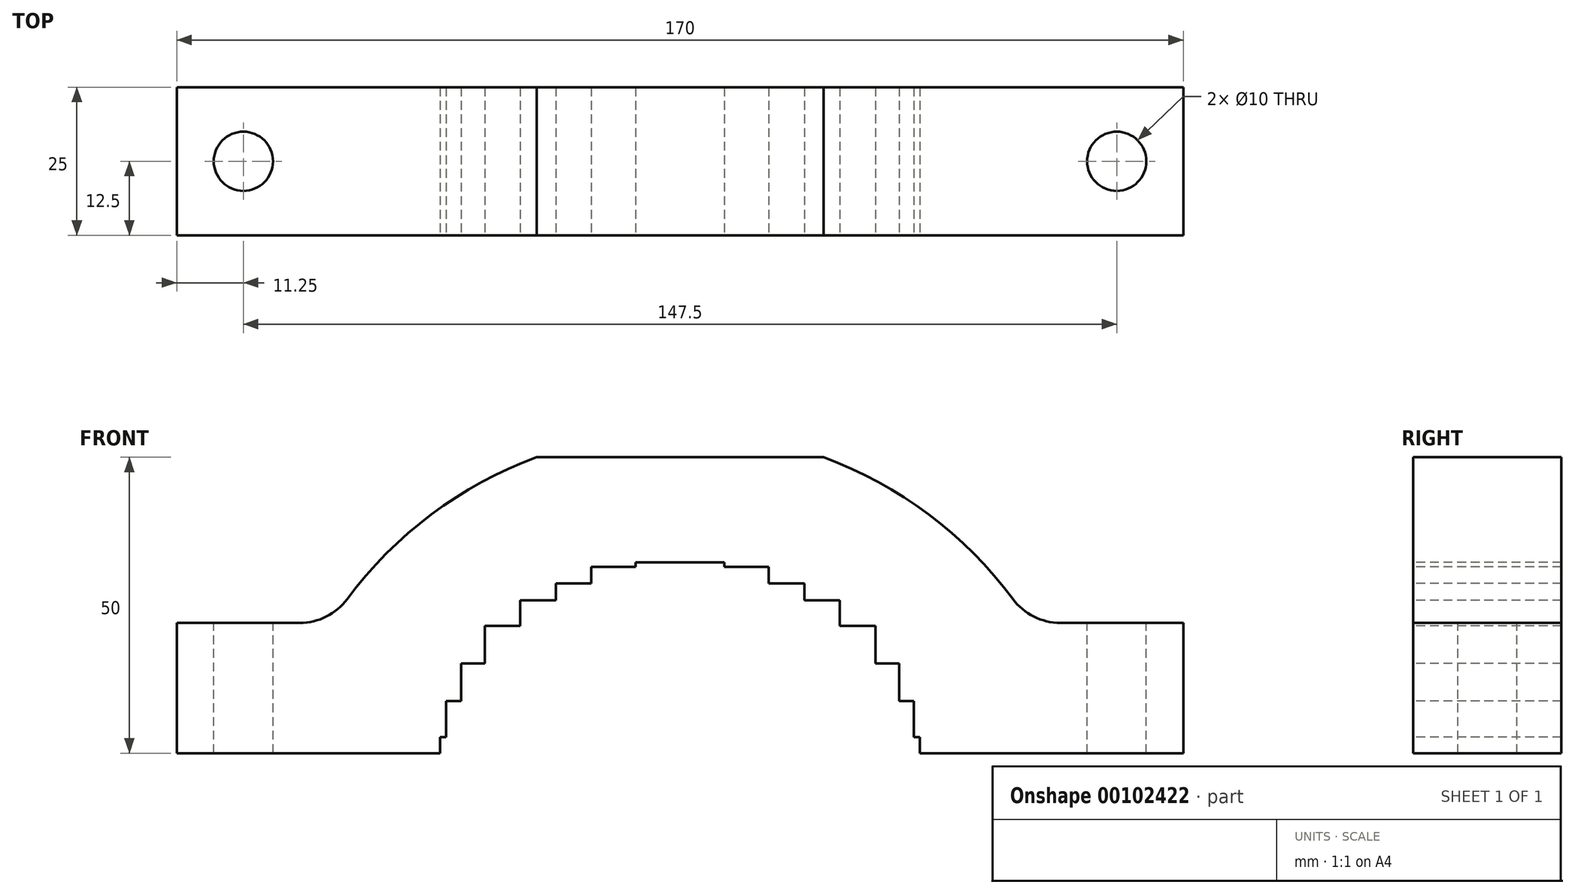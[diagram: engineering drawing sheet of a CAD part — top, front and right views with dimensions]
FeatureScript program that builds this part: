
annotation { "Feature Type Name" : "Feature", "Feature Type Description" : "" }
export const myFeature = defineFeature(function(context is Context, id is Id, definition is map)
    precondition{}
    {
        {
            var Q0;
            Q0=qCreatedBy(makeId("Top.planeOp"),FACE);
            var sketch = newSketch(context, id + "F0", { "sketchPlane" : qUnion([Q0])});
            skLineSegment(sketch, "E0.bottom", {"start": v(0, 0) * mm, "end": v(170, 0) * mm});
            skLineSegment(sketch, "E0.top", {"start": v(0, 25) * mm, "end": v(170, 25) * mm});
            skLineSegment(sketch, "E0.left", {"start": v(0, 0) * mm, "end": v(0, 25) * mm});
            skLineSegment(sketch, "E0.right", {"start": v(170, 0) * mm, "end": v(170, 25) * mm});
            skSolve(sketch);
        }
        {
            var Q0;
            Q0=makeQuery(id+"F0.imprint","IMPRINT",FACE,{"disambiguationData":[TD([[makeQuery(id+"F0.imprint","IMPRINT",EDGE,{"derivedFrom":sQuery(id+"F0.wireOp",EDGE,"E0.bottom")}),1.0]])]});
            extrude(context, id + "F1", {"entities" : qUnion([Q0]), "depth" : 50 * mm});
        }
        {
            var Q0;
            Q0=makeQuery(id+"F1.opExtrude","CAP_FACE",FACE,{"disambiguationData":[OSD([sQuery(id+"F0.wireOp",EDGE,"E0.bottom"),sQuery(id+"F0.wireOp",EDGE,"E0.top"),sQuery(id+"F0.wireOp",EDGE,"E0.left"),sQuery(id+"F0.wireOp",EDGE,"E0.right")])],"isStart":false});
            var sketch = newSketch(context, id + "F2", { "sketchPlane" : qUnion([Q0])});
            skLineSegment(sketch, "E1", {"start": v(0, 12.5) * mm, "end": v(170, 12.5) * mm, "construction": true});
            skLineSegment(sketch, "E2", {"start": v(85, 25) * mm, "end": v(85, 0) * mm, "construction": true});
            skCircle(sketch, "E3", {"center": v(11.25, 12.5) * mm, "radius": 5 * mm});
            skCircle(sketch, "E4.MirrorC", {"center": v(158.75, 12.5) * mm, "radius": 5 * mm});
            skSolve(sketch);
        }
        {
            var Q0;
            Q0 = qSketchRegion(id + "F2", true);
            extrude(context, id + "F3", {"entities" : qUnion([Q0]), "operationType" : NewBodyOperationType.REMOVE, "endBound" : BoundingType.THROUGH_ALL, "oppositeDirection" : true, "depth" : 72.45 * mm});
        }
        {
            var Q0;
            Q0=makeQuery(id+"F1.opExtrude","SWEPT_FACE",FACE,{"disambiguationData":[OSD([sQuery(id+"F0.wireOp",EDGE,"E0.bottom")])]});
            var sketch = newSketch(context, id + "F4", { "sketchPlane" : qUnion([Q0])});
            skLineSegment(sketch, "E5", {"start": v(85, 0) * mm, "end": v(85, 50) * mm, "construction": true});
            skLineSegment(sketch, "E6", {"start": v(85, 0) * mm, "end": v(85, -49.82) * mm, "construction": true});
            skCircle(sketch, "E7", {"center": v(85, -10) * mm, "radius": 41.5 * mm, "construction": true});
            skLineSegment(sketch, "E8", {"start": v(92.5, 31.5) * mm, "end": v(100, 31.5) * mm});
            skLineSegment(sketch, "E9", {"start": v(100, 31.5) * mm, "end": v(100, 28.7) * mm});
            skLineSegment(sketch, "E10", {"start": v(100, 28.7) * mm, "end": v(106, 28.7) * mm});
            skLineSegment(sketch, "E11", {"start": v(106, 28.7) * mm, "end": v(106, 25.8) * mm});
            skLineSegment(sketch, "E12", {"start": v(106, 25.8) * mm, "end": v(112, 25.8) * mm});
            skLineSegment(sketch, "E13", {"start": v(112, 25.8) * mm, "end": v(112, 21.52) * mm});
            skLineSegment(sketch, "E14", {"start": v(112, 21.52) * mm, "end": v(118, 21.52) * mm});
            skLineSegment(sketch, "E15", {"start": v(118, 21.52) * mm, "end": v(118, 15.16) * mm});
            skLineSegment(sketch, "E16", {"start": v(118, 15.16) * mm, "end": v(122, 15.16) * mm});
            skLineSegment(sketch, "E17", {"start": v(122, 15.16) * mm, "end": v(122, 8.8) * mm});
            skLineSegment(sketch, "E18", {"start": v(122, 8.8) * mm, "end": v(124.5, 8.8) * mm});
            skLineSegment(sketch, "E19", {"start": v(124.5, 8.8) * mm, "end": v(124.5, 2.73) * mm});
            skLineSegment(sketch, "E20", {"start": v(124.5, 2.73) * mm, "end": v(125.5, 2.73) * mm});
            skLineSegment(sketch, "E21", {"start": v(125.5, 2.73) * mm, "end": v(125.5, 0) * mm});
            skLineSegment(sketch, "E22", {"start": v(92.5, 31.5) * mm, "end": v(92.5, 32.22) * mm});
            skLineSegment(sketch, "E23", {"start": v(92.5, 32.22) * mm, "end": v(85, 32.22) * mm});
            skPoint(sketch, "E24.orphan", {"position": v(85, 31.5) * mm});
            skLineSegment(sketch, "E25.MirrorCS", {"start": v(64, 28.7) * mm, "end": v(64, 25.8) * mm});
            skLineSegment(sketch, "E26.MirrorCS", {"start": v(45.5, 2.73) * mm, "end": v(44.5, 2.73) * mm});
            skLineSegment(sketch, "E27.MirrorCS", {"start": v(77.5, 31.5) * mm, "end": v(77.5, 32.22) * mm});
            skLineSegment(sketch, "E28.MirrorCS", {"start": v(48, 8.8) * mm, "end": v(45.5, 8.8) * mm});
            skLineSegment(sketch, "E29.MirrorCS", {"start": v(44.5, 2.73) * mm, "end": v(44.5, 0) * mm});
            skLineSegment(sketch, "E30.MirrorCS", {"start": v(77.5, 32.22) * mm, "end": v(85, 32.22) * mm});
            skLineSegment(sketch, "E31.MirrorCS", {"start": v(45.5, 8.8) * mm, "end": v(45.5, 2.73) * mm});
            skLineSegment(sketch, "E32.MirrorCS", {"start": v(64, 25.8) * mm, "end": v(58, 25.8) * mm});
            skLineSegment(sketch, "E33.MirrorCS", {"start": v(77.5, 31.5) * mm, "end": v(70, 31.5) * mm});
            skLineSegment(sketch, "E34.MirrorCS", {"start": v(58, 25.8) * mm, "end": v(58, 21.52) * mm});
            skLineSegment(sketch, "E35.MirrorCS", {"start": v(70, 31.5) * mm, "end": v(70, 28.7) * mm});
            skLineSegment(sketch, "E36.MirrorCS", {"start": v(58, 21.52) * mm, "end": v(52, 21.52) * mm});
            skLineSegment(sketch, "E37.MirrorCS", {"start": v(52, 21.52) * mm, "end": v(52, 15.16) * mm});
            skLineSegment(sketch, "E38.MirrorCS", {"start": v(52, 15.16) * mm, "end": v(48, 15.16) * mm});
            skLineSegment(sketch, "E39.MirrorCS", {"start": v(70, 28.7) * mm, "end": v(64, 28.7) * mm});
            skLineSegment(sketch, "E40.MirrorCS", {"start": v(48, 15.16) * mm, "end": v(48, 8.8) * mm});
            skLineSegment(sketch, "E41", {"start": v(44.5, 0) * mm, "end": v(125.5, 0) * mm});
            skSolve(sketch);
        }
        {
            var Q0;
            Q0=makeQuery(id+"F4.imprint","IMPRINT",FACE,{"disambiguationData":[TD([[makeQuery(id+"F4.imprint","IMPRINT",EDGE,{"derivedFrom":sQuery(id+"F4.wireOp",EDGE,"E8")}),-1.0]])]});
            extrude(context, id + "F5", {"entities" : qUnion([Q0]), "operationType" : NewBodyOperationType.REMOVE, "endBound" : BoundingType.THROUGH_ALL, "oppositeDirection" : true, "depth" : 25 * mm});
        }
        {
            var Q0;
            Q0=makeQuery(id+"F1.opExtrude","SWEPT_FACE",FACE,{"disambiguationData":[OSD([sQuery(id+"F0.wireOp",EDGE,"E0.top")])]});
            var sketch = newSketch(context, id + "F6", { "sketchPlane" : qUnion([Q0])});
            skLineSegment(sketch, "E42", {"start": v(-85, 50) * mm, "end": v(-85, 32.22) * mm, "construction": true});
            skPoint(sketch, "E42.endSnap0", {"position": v(-85, 32.22) * mm});
            skLineSegment(sketch, "E43", {"start": v(-144, 22) * mm, "end": v(-170, 22) * mm});
            skLineSegment(sketch, "E44", {"start": v(-170, 22) * mm, "end": v(-170, 50) * mm});
            skLineSegment(sketch, "E45.MirrorCS", {"start": v(0, 22) * mm, "end": v(0, 50) * mm});
            skLineSegment(sketch, "E46.MirrorCS", {"start": v(-26, 22) * mm, "end": v(0, 22) * mm});
            skArc(sketch, "E47", {"start": v(-26, 22) * mm, "mid": v(-41.09, 38.84) * mm, "end": v(-60.76, 50) * mm});
            skPoint(sketch, "E48.MirrorCS.end.orphan", {"position": v(-50, 50) * mm});
            skPoint(sketch, "E49.end.orphan", {"position": v(-120, 50) * mm});
            skLineSegment(sketch, "E50", {"start": v(-170, 50) * mm, "end": v(-109.24, 50) * mm});
            skArc(sketch, "E51.trimOffspring", {"start": v(-109.24, 50) * mm, "mid": v(-128.91, 38.84) * mm, "end": v(-144, 22) * mm});
            skLineSegment(sketch, "E52.trimOffspring", {"start": v(-60.76, 50) * mm, "end": v(0, 50) * mm});
            skPoint(sketch, "E53.trimOffspring.end.orphan", {"position": v(-85, -19.18) * mm});
            skSolve(sketch);
        }
        {
            var Q0;
            Q0 = qSketchRegion(id + "F6", true);
            extrude(context, id + "F7", {"entities" : qUnion([Q0]), "operationType" : NewBodyOperationType.REMOVE, "endBound" : BoundingType.THROUGH_ALL, "oppositeDirection" : true, "depth" : 25 * mm});
        }
        {
            var Q0;
            Q0=makeQuery(id+"F7.boolean.opBoolean","COPY",EDGE,{"derivedFrom":makeQuery(id+"F7.opExtrude","SWEPT_EDGE",EDGE,{"disambiguationData":[OSD([sQuery(id+"F6.wireOp",EDGE,"E43"),sQuery(id+"F6.wireOp",EDGE,"E51.trimOffspring")])]})});
            var Q1;
            Q1=makeQuery(id+"F7.boolean.opBoolean","COPY",EDGE,{"derivedFrom":makeQuery(id+"F7.opExtrude","SWEPT_EDGE",EDGE,{"disambiguationData":[OSD([sQuery(id+"F6.wireOp",EDGE,"E46.MirrorCS"),sQuery(id+"F6.wireOp",EDGE,"E47")])]})});
            fillet(context, id + "F8", {"entities" : qUnion([Q0, Q1]), "radius" : 10 * mm, "tangentPropagation" : true, "allowEdgeOverflow" : false});
        }
    });
